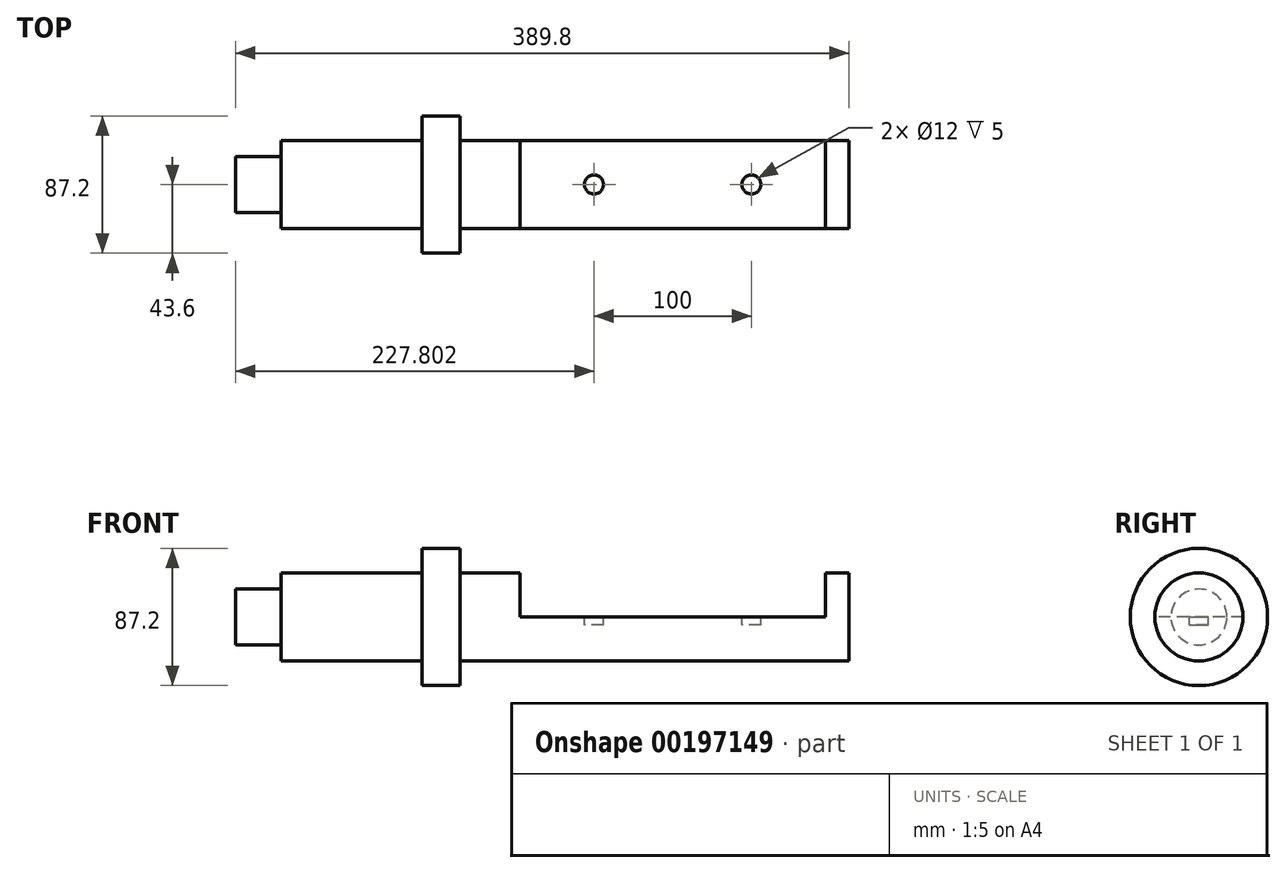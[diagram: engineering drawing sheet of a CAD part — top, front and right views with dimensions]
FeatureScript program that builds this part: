
annotation { "Feature Type Name" : "Feature", "Feature Type Description" : "" }
export const myFeature = defineFeature(function(context is Context, id is Id, definition is map)
    precondition{}
    {
        {
            var Q0;
            Q0=qCreatedBy(makeId("Front.planeOp"),FACE);
            var sketch = newSketch(context, id + "F0", { "sketchPlane" : qUnion([Q0])});
            skLineSegment(sketch, "E0", {"start": v(-74.38, 0) * mm, "end": v(123.48, 0) * mm, "construction": true});
            skLineSegment(sketch, "E1", {"start": v(-44.3, 0) * mm, "end": v(-44.3, 17.75) * mm});
            skLineSegment(sketch, "E2", {"start": v(-44.3, 17.75) * mm, "end": v(-15.4, 17.75) * mm});
            skLineSegment(sketch, "E3", {"start": v(-15.4, 17.75) * mm, "end": v(-15.4, 28) * mm});
            skLineSegment(sketch, "E4", {"start": v(-15.4, 28) * mm, "end": v(74.4, 28) * mm});
            skLineSegment(sketch, "E5", {"start": v(74.4, 28) * mm, "end": v(74.4, 43.6) * mm});
            skLineSegment(sketch, "E6", {"start": v(74.4, 43.6) * mm, "end": v(98.4, 43.6) * mm});
            skLineSegment(sketch, "E7", {"start": v(98.4, 43.6) * mm, "end": v(98.4, 28) * mm});
            skLineSegment(sketch, "E8", {"start": v(98.4, 28) * mm, "end": v(345.5, 28) * mm});
            skLineSegment(sketch, "E9", {"start": v(345.5, 28) * mm, "end": v(345.5, 0) * mm});
            skLineSegment(sketch, "E10", {"start": v(345.5, 0) * mm, "end": v(-44.3, 0) * mm});
            skSolve(sketch);
        }
        {
            var Q0;
            Q0 = qSketchRegion(id + "F0", true);
            var Q1;
            Q1=sQuery(id+"F0.wireOp",EDGE,"E0");
            revolve(context, id + "F1", {"entities" : qUnion([Q0]), "axis" : qUnion([Q1]), "revolveType" : RevolveType.FULL});
        }
        {
            var Q0;
            Q0=qCreatedBy(makeId("Front.planeOp"),FACE);
            var sketch = newSketch(context, id + "F3", { "sketchPlane" : qUnion([Q0])});
            skLineSegment(sketch, "E11.bottom", {"start": v(136.6, 0) * mm, "end": v(330.4, 0) * mm});
            skLineSegment(sketch, "E11.top", {"start": v(136.6, 30.88) * mm, "end": v(330.4, 30.88) * mm});
            skLineSegment(sketch, "E11.left", {"start": v(136.6, 0) * mm, "end": v(136.6, 30.88) * mm});
            skLineSegment(sketch, "E11.right", {"start": v(330.4, 0) * mm, "end": v(330.4, 30.88) * mm});
            skSolve(sketch);
        }
        {
            var Q0;
            Q0 = qSketchRegion(id + "F3", true);
            extrude(context, id + "F2", {"entities" : qUnion([Q0]), "operationType" : NewBodyOperationType.REMOVE, "endBound" : BoundingType.SYMMETRIC, "oppositeDirection" : true, "depth" : 130.71 * mm});
        }
        {
            var Q0;
            Q0=makeQuery(id+"F2.boolean.opBoolean","COPY",FACE,{"derivedFrom":makeQuery(id+"F2.opExtrude","SWEPT_FACE",FACE,{"disambiguationData":[OSD([sQuery(id+"F3.wireOp",EDGE,"E11.bottom")])]})});
            var sketch = newSketch(context, id + "F4", { "sketchPlane" : qUnion([Q0])});
            skLineSegment(sketch, "E12", {"start": v(136.6, 0) * mm, "end": v(330.4, 0) * mm, "construction": true});
            skCircle(sketch, "E13", {"center": v(183.5, 0) * mm, "radius": 6 * mm});
            skCircle(sketch, "E14", {"center": v(283.5, 0) * mm, "radius": 6 * mm});
            skLineSegment(sketch, "E15", {"start": v(233.5, 0) * mm, "end": v(233.5, -28) * mm, "construction": true});
            skSolve(sketch);
        }
        {
            var Q0;
            Q0 = qSketchRegion(id + "F4", true);
            extrude(context, id + "F5", {"entities" : qUnion([Q0]), "operationType" : NewBodyOperationType.REMOVE, "oppositeDirection" : true, "depth" : 5 * mm});
        }
    });
